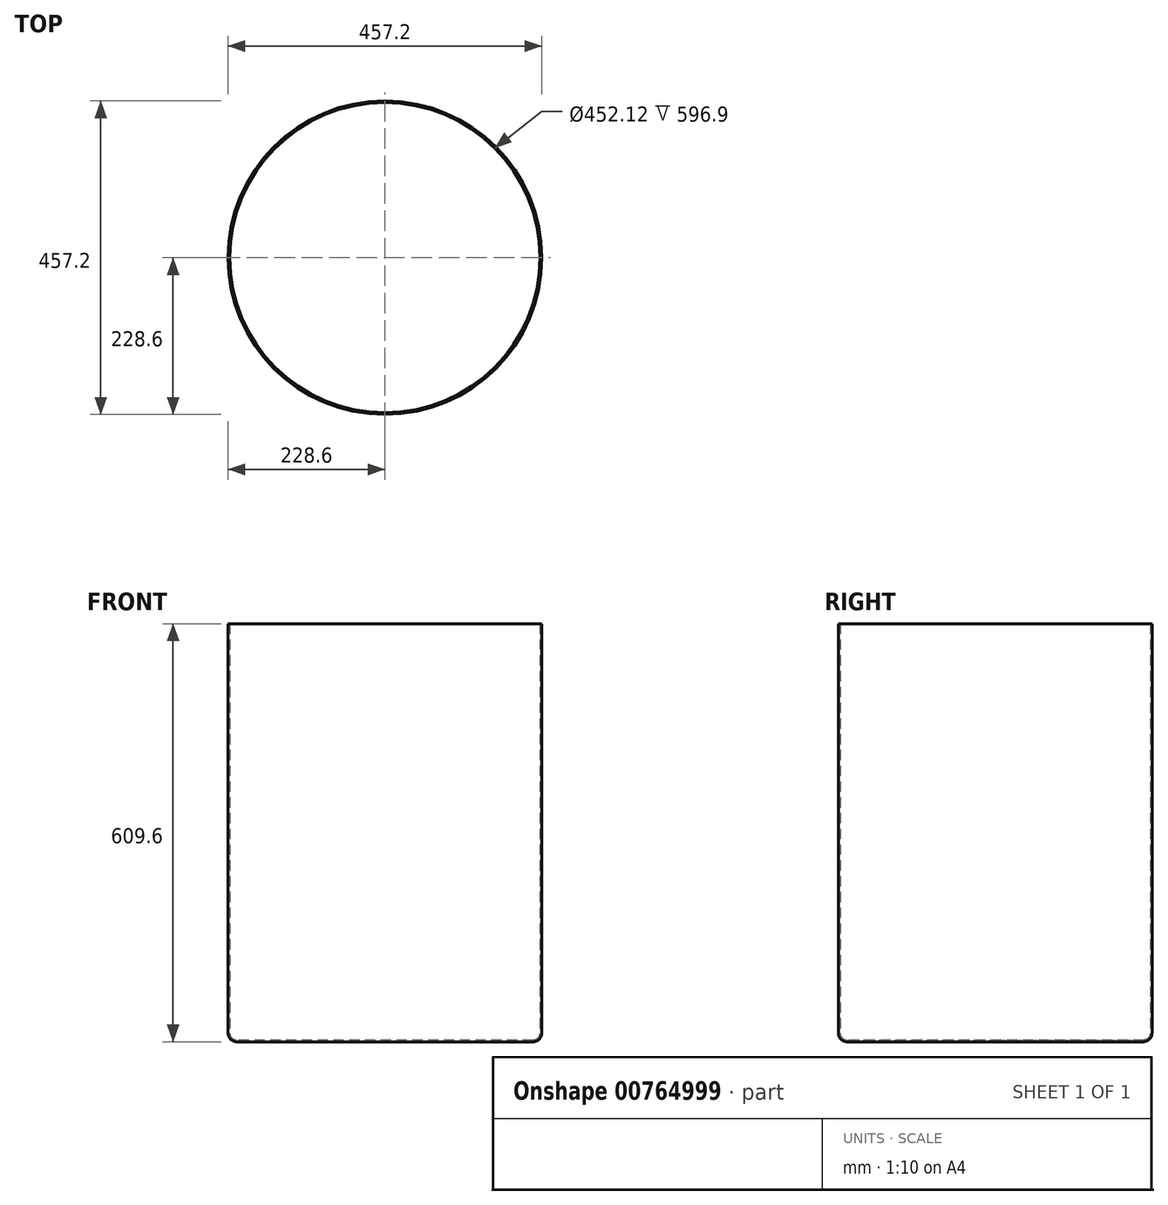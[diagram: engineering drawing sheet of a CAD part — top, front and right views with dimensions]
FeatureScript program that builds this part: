
annotation { "Feature Type Name" : "Feature", "Feature Type Description" : "" }
export const myFeature = defineFeature(function(context is Context, id is Id, definition is map)
    precondition{}
    {
        {
            var Q0;
            Q0=qCreatedBy(makeId("Top.planeOp"),FACE);
            var sketch = newSketch(context, id + "F0", { "sketchPlane" : qUnion([Q0])});
            skCircle(sketch, "E0", {"center": v(0, 0) * mm, "radius": 228.6 * mm});
            skSolve(sketch);
        }
        {
            var Q0;
            Q0 = qSketchRegion(id + "F0", true);
            extrude(context, id + "F1", {"entities" : qUnion([Q0]), "depth" : 609.6 * mm, "offsetDistance" : 25.4 * mm});
        }
        {
            var Q0;
            Q0=makeQuery(id+"F1.opExtrude","CAP_EDGE",EDGE,{"disambiguationData":[OSD([sQuery(id+"F0.wireOp",EDGE,"E0")])],"isStart":true});
            fillet(context, id + "F2", {"entities" : qUnion([Q0]), "radius" : 12.7 * mm, "tangentPropagation" : true, "allowEdgeOverflow" : false});
        }
        {
            var Q0;
            Q0=makeQuery(id+"F1.opExtrude","CAP_FACE",FACE,{"disambiguationData":[OSD([sQuery(id+"F0.wireOp",EDGE,"E0")])],"isStart":false});
            shell(context, id + "F3", {"entities" : qUnion([Q0]), "thickness" : 2.54 * mm});
        }
    });
